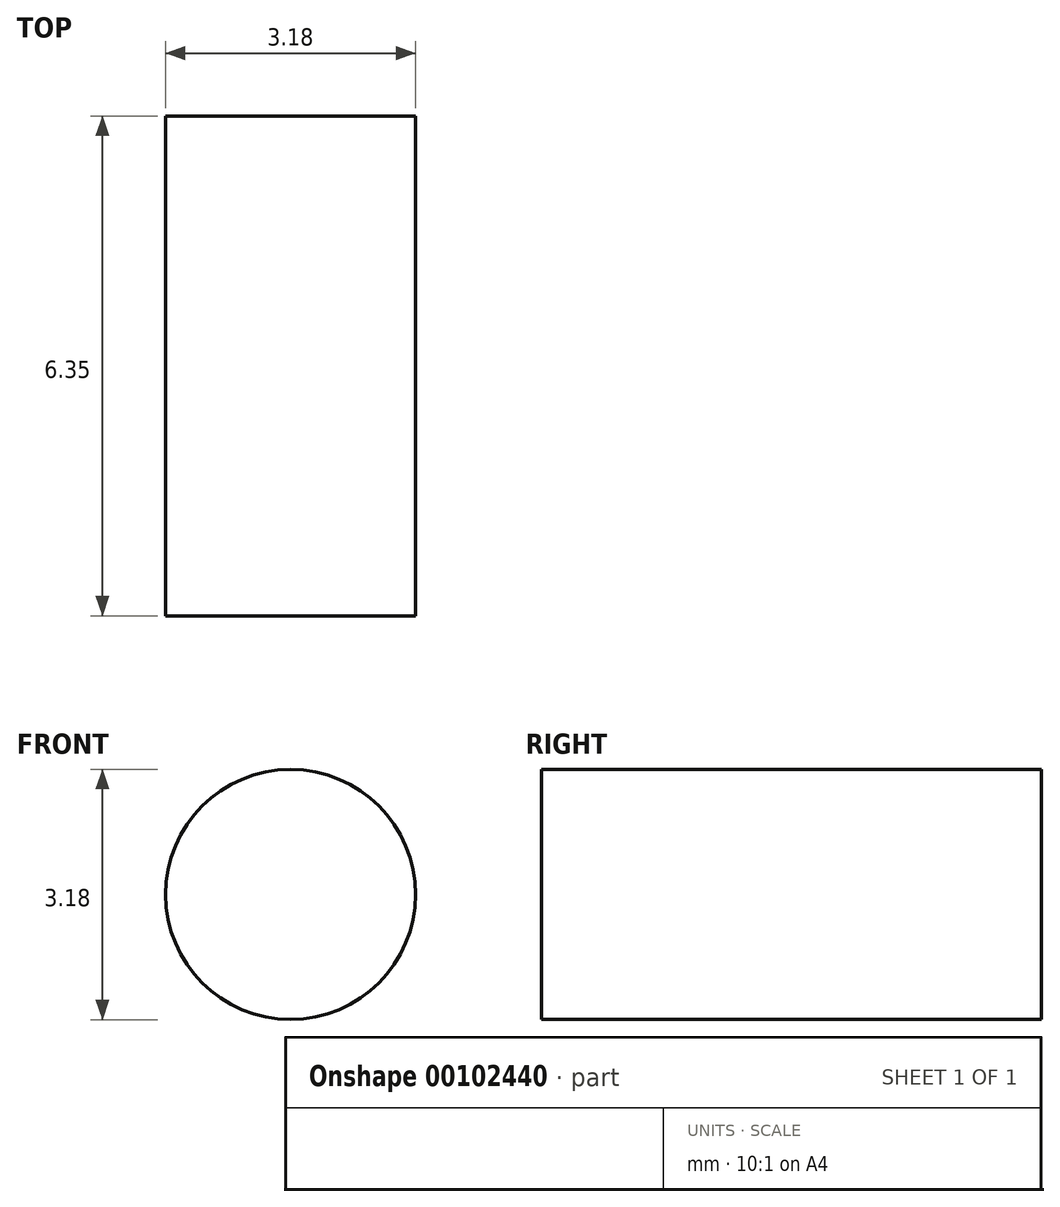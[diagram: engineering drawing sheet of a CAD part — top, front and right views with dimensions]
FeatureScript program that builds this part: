
annotation { "Feature Type Name" : "Feature", "Feature Type Description" : "" }
export const myFeature = defineFeature(function(context is Context, id is Id, definition is map)
    precondition{}
    {
        {
            var Q0;
            Q0=qCreatedBy(makeId("Front.planeOp"),FACE);
            var sketch = newSketch(context, id + "F0", { "sketchPlane" : qUnion([Q0])});
            skCircle(sketch, "E0", {"center": v(0, 0) * mm, "radius": 1.59 * mm});
            skSolve(sketch);
        }
        {
            var Q0;
            Q0=makeQuery(id+"F0.imprint","IMPRINT",FACE,{"disambiguationData":[TD([[makeQuery(id+"F0.imprint","IMPRINT",EDGE,{"derivedFrom":sQuery(id+"F0.wireOp",EDGE,"E0")}),1.0]])]});
            extrude(context, id + "F1", {"entities" : qUnion([Q0]), "depth" : 6.35 * mm});
        }
    });
